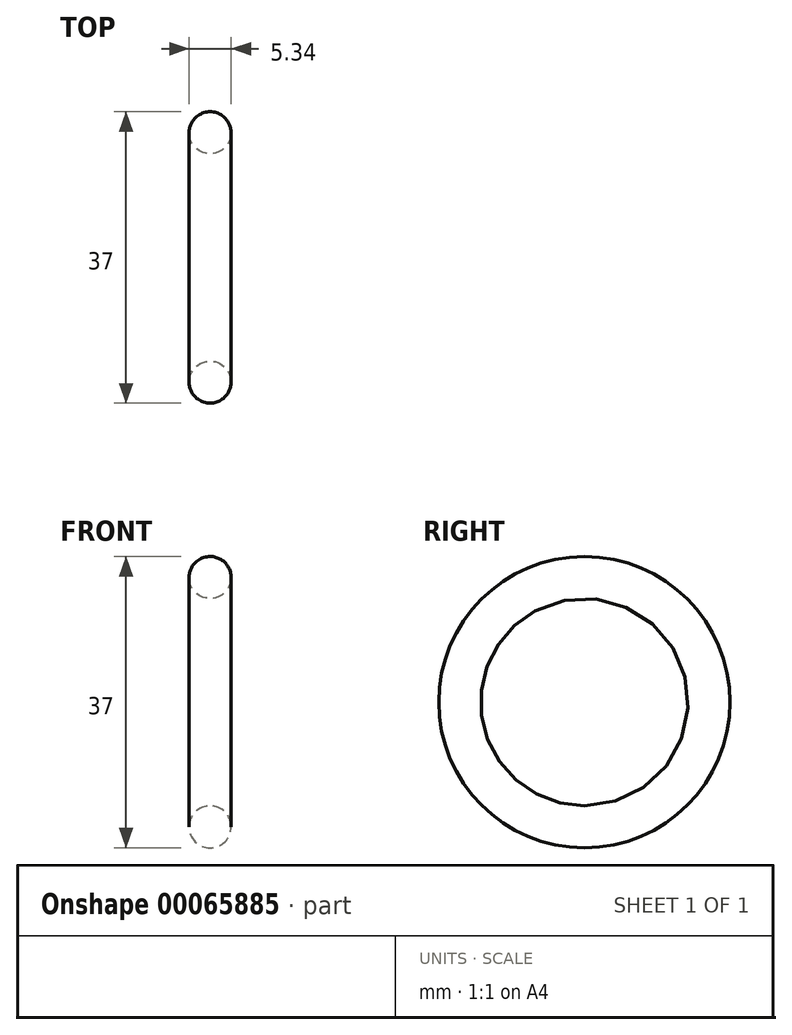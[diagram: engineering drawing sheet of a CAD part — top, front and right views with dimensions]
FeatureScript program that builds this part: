
annotation { "Feature Type Name" : "Feature", "Feature Type Description" : "" }
export const myFeature = defineFeature(function(context is Context, id is Id, definition is map)
    precondition{}
    {
        {
            var Q0;
            Q0=qCreatedBy(makeId("Front.planeOp"),FACE);
            var sketch = newSketch(context, id + "F0", { "sketchPlane" : qUnion([Q0])});
            skLineSegment(sketch, "E0", {"start": v(0, 0) * mm, "end": v(-6.06, 0) * mm, "construction": true});
            skCircle(sketch, "E1", {"center": v(0, 15.84) * mm, "radius": 2.67 * mm});
            skSolve(sketch);
        }
        {
            var Q0;
            Q0=makeQuery(id+"F0.imprint","IMPRINT",FACE,{"disambiguationData":[TD([[makeQuery(id+"F0.imprint","IMPRINT",EDGE,{"derivedFrom":sQuery(id+"F0.wireOp",EDGE,"E1")}),1.0]])]});
            var Q1;
            Q1=sQuery(id+"F0.wireOp",EDGE,"E0");
            revolve(context, id + "F1", {"entities" : qUnion([Q0]), "axis" : qUnion([Q1]), "revolveType" : RevolveType.FULL});
        }
    });
